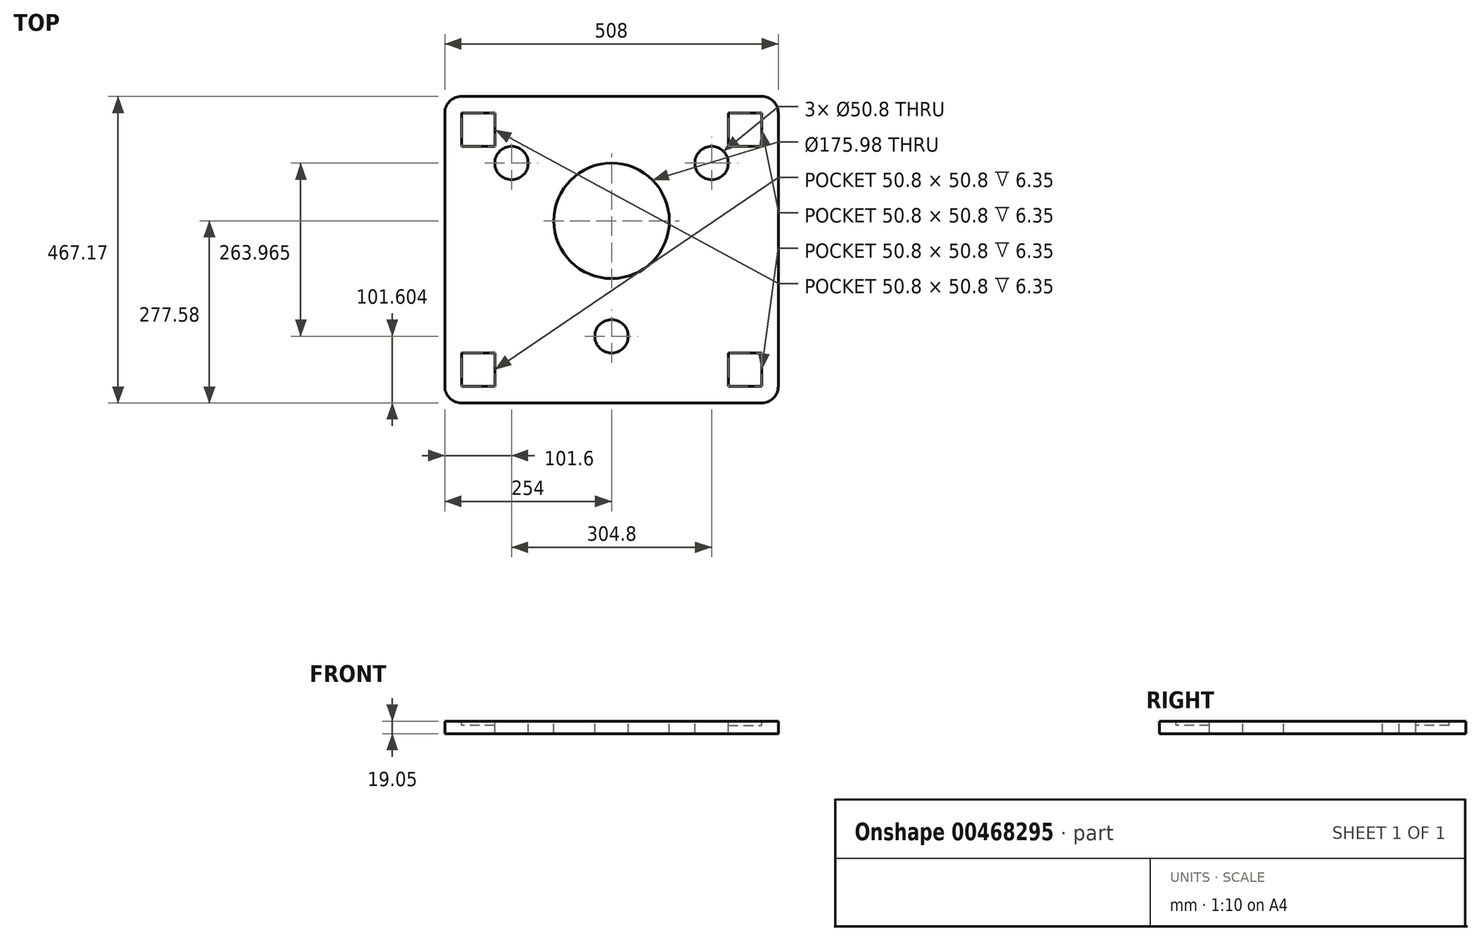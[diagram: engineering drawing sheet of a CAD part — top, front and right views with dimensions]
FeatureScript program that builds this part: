
annotation { "Feature Type Name" : "Feature", "Feature Type Description" : "" }
export const myFeature = defineFeature(function(context is Context, id is Id, definition is map)
    precondition{}
    {
        {
            var Q0;
            Q0=qCreatedBy(makeId("Top.planeOp"),FACE);
            var sketch = newSketch(context, id + "F0", { "sketchPlane" : qUnion([Q0])});
            skCircle(sketch, "E0", {"center": v(0, 0) * mm, "radius": 87.99 * mm});
            skLineSegment(sketch, "E1", {"start": v(-152.4, 87.99) * mm, "end": v(152.4, 87.99) * mm, "construction": true});
            skLineSegment(sketch, "E2", {"start": v(152.4, 87.99) * mm, "end": v(0, -175.98) * mm, "construction": true});
            skLineSegment(sketch, "E3", {"start": v(0, -175.98) * mm, "end": v(-152.4, 87.99) * mm, "construction": true});
            skCircle(sketch, "E4", {"center": v(-152.4, 87.99) * mm, "radius": 25.4 * mm});
            skCircle(sketch, "E5", {"center": v(152.4, 87.99) * mm, "radius": 25.4 * mm});
            skCircle(sketch, "E6", {"center": v(0, -175.98) * mm, "radius": 25.4 * mm});
            skLineSegment(sketch, "E7.bottom", {"start": v(-254, 189.59) * mm, "end": v(254, 189.59) * mm});
            skLineSegment(sketch, "E7.top", {"start": v(-254, -277.58) * mm, "end": v(254, -277.58) * mm});
            skLineSegment(sketch, "E7.left", {"start": v(-254, 189.59) * mm, "end": v(-254, -277.58) * mm});
            skLineSegment(sketch, "E7.right", {"start": v(254, 189.59) * mm, "end": v(254, -277.58) * mm});
            skLineSegment(sketch, "E8.bottom", {"start": v(-228.6, 164.19) * mm, "end": v(-177.8, 164.19) * mm});
            skLineSegment(sketch, "E8.top", {"start": v(-228.6, 113.39) * mm, "end": v(-177.8, 113.39) * mm});
            skLineSegment(sketch, "E8.left", {"start": v(-228.6, 164.19) * mm, "end": v(-228.6, 113.39) * mm});
            skLineSegment(sketch, "E8.right", {"start": v(-177.8, 164.19) * mm, "end": v(-177.8, 113.39) * mm});
            skLineSegment(sketch, "E9.bottom", {"start": v(177.8, 164.19) * mm, "end": v(228.6, 164.19) * mm});
            skLineSegment(sketch, "E9.top", {"start": v(177.8, 113.39) * mm, "end": v(228.6, 113.39) * mm});
            skLineSegment(sketch, "E9.left", {"start": v(177.8, 164.19) * mm, "end": v(177.8, 113.39) * mm});
            skLineSegment(sketch, "E9.right", {"start": v(228.6, 164.19) * mm, "end": v(228.6, 113.39) * mm});
            skLineSegment(sketch, "E10.bottom", {"start": v(177.8, -201.38) * mm, "end": v(228.6, -201.38) * mm});
            skLineSegment(sketch, "E10.top", {"start": v(177.8, -252.18) * mm, "end": v(228.6, -252.18) * mm});
            skLineSegment(sketch, "E10.left", {"start": v(177.8, -201.38) * mm, "end": v(177.8, -252.18) * mm});
            skLineSegment(sketch, "E10.right", {"start": v(228.6, -201.38) * mm, "end": v(228.6, -252.18) * mm});
            skLineSegment(sketch, "E11.bottom", {"start": v(-177.8, -201.38) * mm, "end": v(-228.6, -201.38) * mm});
            skLineSegment(sketch, "E11.top", {"start": v(-177.8, -252.18) * mm, "end": v(-228.6, -252.18) * mm});
            skLineSegment(sketch, "E11.left", {"start": v(-177.8, -201.38) * mm, "end": v(-177.8, -252.18) * mm});
            skLineSegment(sketch, "E11.right", {"start": v(-228.6, -201.38) * mm, "end": v(-228.6, -252.18) * mm});
            skSolve(sketch);
        }
        {
            var Q0;
            Q0=makeQuery(id+"F0.imprint","IMPRINT",FACE,{"disambiguationData":[TD([[makeQuery(id+"F0.imprint","IMPRINT",EDGE,{"derivedFrom":sQuery(id+"F0.wireOp",EDGE,"E0")}),-1.0]])]});
            var Q1;
            Q1=makeQuery(id+"F0.imprint","IMPRINT",FACE,{"disambiguationData":[TD([[makeQuery(id+"F0.imprint","IMPRINT",EDGE,{"derivedFrom":sQuery(id+"F0.wireOp",EDGE,"E8.bottom")}),-1.0]])]});
            var Q2;
            Q2=makeQuery(id+"F0.imprint","IMPRINT",FACE,{"disambiguationData":[TD([[makeQuery(id+"F0.imprint","IMPRINT",EDGE,{"derivedFrom":sQuery(id+"F0.wireOp",EDGE,"E11.bottom")}),1.0]])]});
            var Q3;
            Q3=makeQuery(id+"F0.imprint","IMPRINT",FACE,{"disambiguationData":[TD([[makeQuery(id+"F0.imprint","IMPRINT",EDGE,{"derivedFrom":sQuery(id+"F0.wireOp",EDGE,"E10.bottom")}),-1.0]])]});
            var Q4;
            Q4=makeQuery(id+"F0.imprint","IMPRINT",FACE,{"disambiguationData":[TD([[makeQuery(id+"F0.imprint","IMPRINT",EDGE,{"derivedFrom":sQuery(id+"F0.wireOp",EDGE,"E9.bottom")}),-1.0]])]});
            var Q5;
            Q5=makeQuery(id+"F0.imprint","IMPRINT",FACE,{"disambiguationData":[TD([[makeQuery(id+"F0.imprint","IMPRINT",EDGE,{"derivedFrom":sQuery(id+"F0.wireOp",EDGE,"E4")}),1.0]])]});
            var Q6;
            Q6=makeQuery(id+"F0.imprint","IMPRINT",FACE,{"disambiguationData":[TD([[makeQuery(id+"F0.imprint","IMPRINT",EDGE,{"derivedFrom":sQuery(id+"F0.wireOp",EDGE,"E5")}),1.0]])]});
            var Q7;
            Q7=makeQuery(id+"F0.imprint","IMPRINT",FACE,{"disambiguationData":[TD([[makeQuery(id+"F0.imprint","IMPRINT",EDGE,{"derivedFrom":sQuery(id+"F0.wireOp",EDGE,"E6")}),1.0]])]});
            extrude(context, id + "F1", {"entities" : qUnion([Q0, Q1, Q2, Q3, Q4, Q5, Q6, Q7]), "oppositeDirection" : true, "depth" : 19.05 * mm});
        }
        {
            var Q0;
            Q0=makeQuery(id+"F1.opExtrude","SWEPT_EDGE",EDGE,{"disambiguationData":[OSD([sQuery(id+"F0.wireOp",EDGE,"E7.bottom"),sQuery(id+"F0.wireOp",EDGE,"E7.left")])]});
            var Q1;
            Q1=makeQuery(id+"F1.opExtrude","SWEPT_EDGE",EDGE,{"disambiguationData":[OSD([sQuery(id+"F0.wireOp",EDGE,"E7.bottom"),sQuery(id+"F0.wireOp",EDGE,"E7.right")])]});
            var Q2;
            Q2=makeQuery(id+"F1.opExtrude","SWEPT_EDGE",EDGE,{"disambiguationData":[OSD([sQuery(id+"F0.wireOp",EDGE,"E7.top"),sQuery(id+"F0.wireOp",EDGE,"E7.left")])]});
            var Q3;
            Q3=makeQuery(id+"F1.opExtrude","SWEPT_EDGE",EDGE,{"disambiguationData":[OSD([sQuery(id+"F0.wireOp",EDGE,"E7.top"),sQuery(id+"F0.wireOp",EDGE,"E7.right")])]});
            fillet(context, id + "F2", {"entities" : qUnion([Q0, Q1, Q2, Q3]), "radius" : 25.4 * mm, "tangentPropagation" : true, "allowEdgeOverflow" : false});
        }
        {
            var Q0;
            Q0=makeQuery(id+"F0.imprint","IMPRINT",FACE,{"disambiguationData":[TD([[makeQuery(id+"F0.imprint","IMPRINT",EDGE,{"derivedFrom":sQuery(id+"F0.wireOp",EDGE,"E11.bottom")}),1.0]])]});
            var Q1;
            Q1=makeQuery(id+"F0.imprint","IMPRINT",FACE,{"disambiguationData":[TD([[makeQuery(id+"F0.imprint","IMPRINT",EDGE,{"derivedFrom":sQuery(id+"F0.wireOp",EDGE,"E8.bottom")}),-1.0]])]});
            var Q2;
            Q2=makeQuery(id+"F0.imprint","IMPRINT",FACE,{"disambiguationData":[TD([[makeQuery(id+"F0.imprint","IMPRINT",EDGE,{"derivedFrom":sQuery(id+"F0.wireOp",EDGE,"E10.bottom")}),-1.0]])]});
            var Q3;
            Q3=makeQuery(id+"F0.imprint","IMPRINT",FACE,{"disambiguationData":[TD([[makeQuery(id+"F0.imprint","IMPRINT",EDGE,{"derivedFrom":sQuery(id+"F0.wireOp",EDGE,"E9.bottom")}),-1.0]])]});
            extrude(context, id + "F3", {"entities" : qUnion([Q0, Q1, Q2, Q3]), "operationType" : NewBodyOperationType.REMOVE, "oppositeDirection" : true, "depth" : 6.35 * mm});
        }
        {
            var Q0;
            Q0=makeQuery(id+"F0.imprint","IMPRINT",FACE,{"disambiguationData":[TD([[makeQuery(id+"F0.imprint","IMPRINT",EDGE,{"derivedFrom":sQuery(id+"F0.wireOp",EDGE,"E4")}),1.0]])]});
            var Q1;
            Q1=makeQuery(id+"F0.imprint","IMPRINT",FACE,{"disambiguationData":[TD([[makeQuery(id+"F0.imprint","IMPRINT",EDGE,{"derivedFrom":sQuery(id+"F0.wireOp",EDGE,"E6")}),1.0]])]});
            var Q2;
            Q2=makeQuery(id+"F0.imprint","IMPRINT",FACE,{"disambiguationData":[TD([[makeQuery(id+"F0.imprint","IMPRINT",EDGE,{"derivedFrom":sQuery(id+"F0.wireOp",EDGE,"E5")}),1.0]])]});
            extrude(context, id + "F4", {"entities" : qUnion([Q0, Q1, Q2]), "operationType" : NewBodyOperationType.REMOVE, "endBound" : BoundingType.THROUGH_ALL, "oppositeDirection" : true, "depth" : 25 * mm});
        }
    });
